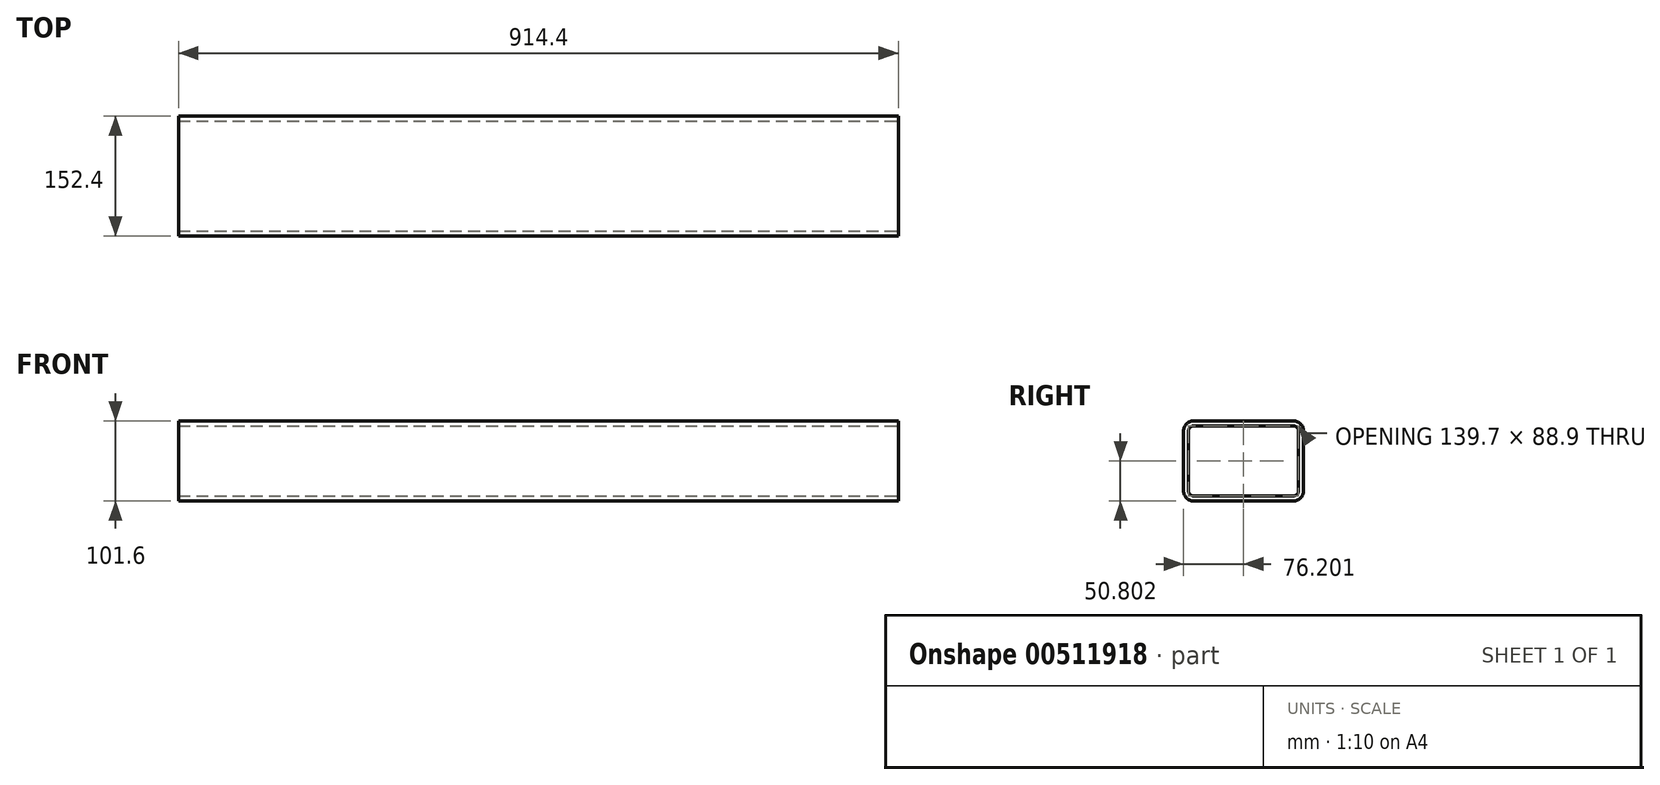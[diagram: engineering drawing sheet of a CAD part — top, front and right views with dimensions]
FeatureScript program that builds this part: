
annotation { "Feature Type Name" : "Feature", "Feature Type Description" : "" }
export const myFeature = defineFeature(function(context is Context, id is Id, definition is map)
    precondition{}
    {
        {
            var Q0;
            Q0=qCreatedBy(makeId("Right.planeOp"),FACE);
            var sketch = newSketch(context, id + "F0", { "sketchPlane" : qUnion([Q0])});
            skLineSegment(sketch, "E0.bottom", {"start": v(-68.5, 15.76) * mm, "end": v(58.5, 15.76) * mm});
            skLineSegment(sketch, "E0.top", {"start": v(-68.5, 117.36) * mm, "end": v(58.5, 117.36) * mm});
            skLineSegment(sketch, "E0.left", {"start": v(-81.2, 28.46) * mm, "end": v(-81.2, 104.66) * mm});
            skLineSegment(sketch, "E0.right", {"start": v(71.2, 28.46) * mm, "end": v(71.2, 104.66) * mm});
            skPoint(sketch, "E1.visualSharp", {"position": v(-81.2, 117.36) * mm});
            skArc(sketch, "E1.filletArc", {"start": v(-68.5, 117.36) * mm, "mid": v(-77.48, 113.64) * mm, "end": v(-81.2, 104.66) * mm});
            skPoint(sketch, "E2.visualSharp", {"position": v(71.2, 117.36) * mm});
            skArc(sketch, "E2.filletArc", {"start": v(71.2, 104.66) * mm, "mid": v(67.48, 113.64) * mm, "end": v(58.5, 117.36) * mm});
            skPoint(sketch, "E3.visualSharp", {"position": v(71.2, 15.76) * mm});
            skArc(sketch, "E3.filletArc", {"start": v(58.5, 15.76) * mm, "mid": v(67.48, 19.48) * mm, "end": v(71.2, 28.46) * mm});
            skPoint(sketch, "E4.visualSharp", {"position": v(-81.2, 15.76) * mm});
            skArc(sketch, "E4.filletArc", {"start": v(-81.2, 28.46) * mm, "mid": v(-77.48, 19.48) * mm, "end": v(-68.5, 15.76) * mm});
            skSolve(sketch);
        }
        {
            var Q0;
            Q0=makeQuery(id+"F0.imprint","IMPRINT",FACE,{"disambiguationData":[TD([[makeQuery(id+"F0.imprint","IMPRINT",EDGE,{"derivedFrom":sQuery(id+"F0.wireOp",EDGE,"E0.bottom")}),1.0]])]});
            extrude(context, id + "F1", {"entities" : qUnion([Q0]), "oppositeDirection" : true, "depth" : 914.4 * mm});
        }
        {
            var Q0;
            Q0=makeQuery(id+"F1.opExtrude","CAP_FACE",FACE,{"disambiguationData":[OSD([sQuery(id+"F0.wireOp",EDGE,"E0.bottom"),sQuery(id+"F0.wireOp",EDGE,"E0.top"),sQuery(id+"F0.wireOp",EDGE,"E0.left"),sQuery(id+"F0.wireOp",EDGE,"E0.right")])],"isStart":true});
            var sketch = newSketch(context, id + "F2", { "sketchPlane" : qUnion([Q0])});
            skLineSegment(sketch, "E5.bottom", {"start": v(-68.5, 22.11) * mm, "end": v(58.5, 22.11) * mm});
            skLineSegment(sketch, "E5.top", {"start": v(-68.5, 111.01) * mm, "end": v(58.5, 111.01) * mm});
            skLineSegment(sketch, "E5.left", {"start": v(-74.85, 28.46) * mm, "end": v(-74.85, 104.66) * mm});
            skLineSegment(sketch, "E5.right", {"start": v(64.85, 28.46) * mm, "end": v(64.85, 104.66) * mm});
            skPoint(sketch, "E6.visualSharp", {"position": v(-74.85, 111.01) * mm});
            skArc(sketch, "E6.filletArc", {"start": v(-68.5, 111.01) * mm, "mid": v(-72.99, 109.15) * mm, "end": v(-74.85, 104.66) * mm});
            skPoint(sketch, "E7.visualSharp", {"position": v(64.85, 111.01) * mm});
            skArc(sketch, "E7.filletArc", {"start": v(64.85, 104.66) * mm, "mid": v(63, 109.15) * mm, "end": v(58.5, 111.01) * mm});
            skPoint(sketch, "E8.visualSharp", {"position": v(64.85, 22.11) * mm});
            skArc(sketch, "E8.filletArc", {"start": v(58.5, 22.11) * mm, "mid": v(63, 23.97) * mm, "end": v(64.85, 28.46) * mm});
            skPoint(sketch, "E9.visualSharp", {"position": v(-74.85, 22.11) * mm});
            skArc(sketch, "E9.filletArc", {"start": v(-74.85, 28.46) * mm, "mid": v(-72.99, 23.97) * mm, "end": v(-68.5, 22.11) * mm});
            skSolve(sketch);
        }
        {
            var Q0;
            Q0 = qSketchRegion(id + "F2", true);
            extrude(context, id + "F3", {"entities" : qUnion([Q0]), "operationType" : NewBodyOperationType.REMOVE, "endBound" : BoundingType.THROUGH_ALL, "oppositeDirection" : true, "depth" : 25.4 * mm});
        }
    });
